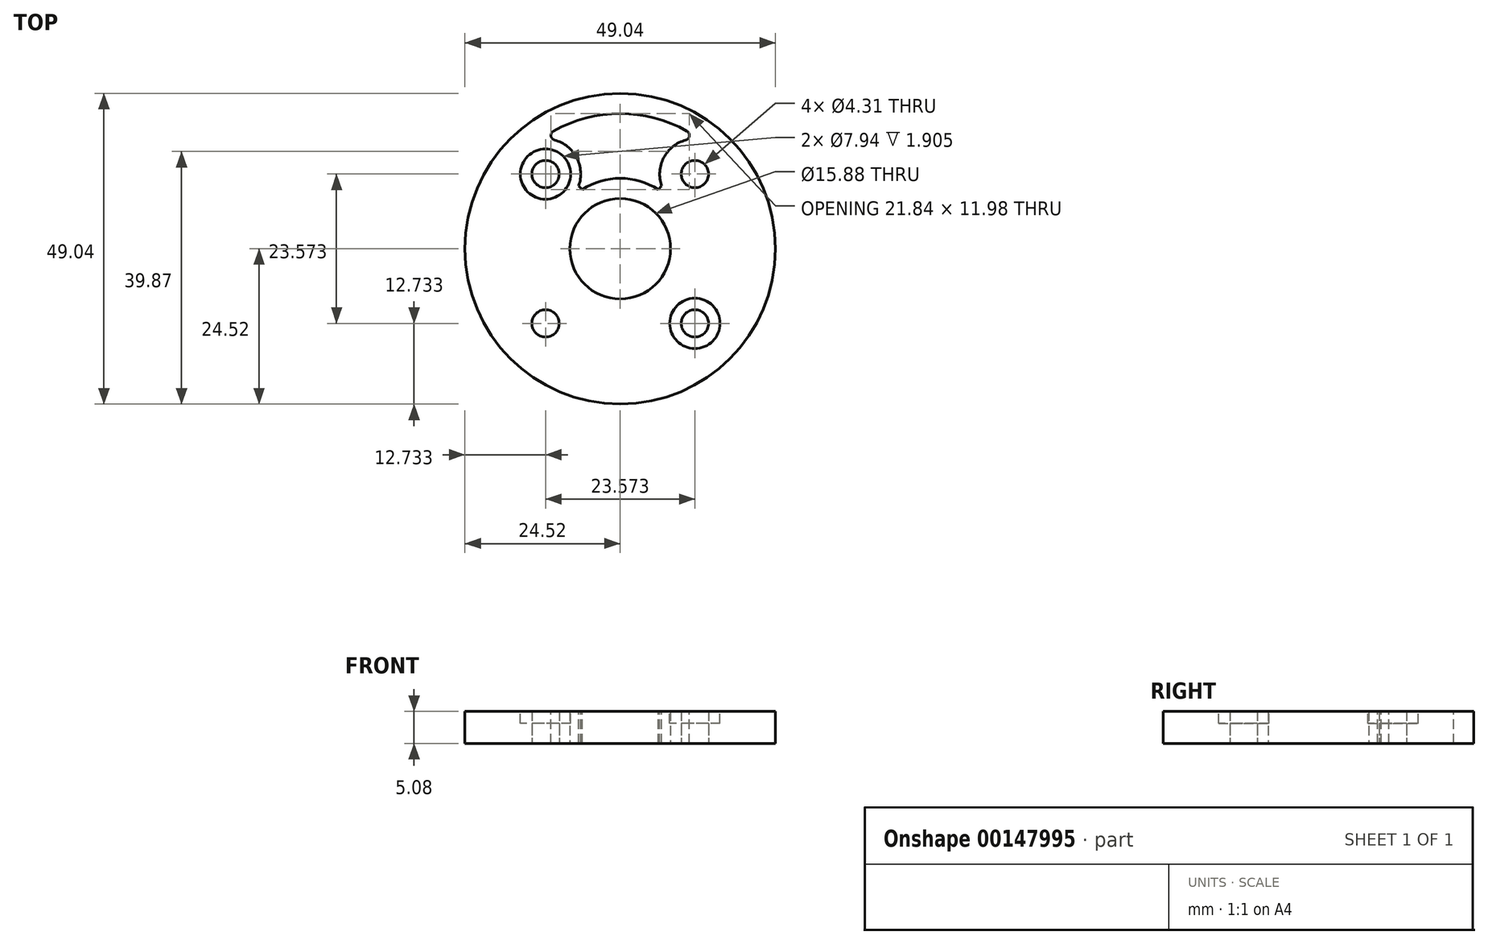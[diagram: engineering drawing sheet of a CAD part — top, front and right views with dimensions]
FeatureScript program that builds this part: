
annotation { "Feature Type Name" : "Feature", "Feature Type Description" : "" }
export const myFeature = defineFeature(function(context is Context, id is Id, definition is map)
    precondition{}
    {
        {
            var Q0;
            Q0=qCreatedBy(makeId("Top.planeOp"),FACE);
            var sketch = newSketch(context, id + "F0", { "sketchPlane" : qUnion([Q0])});
            skCircle(sketch, "E0", {"center": v(0, 0) * mm, "radius": 24.52 * mm});
            skCircle(sketch, "E1", {"center": v(0, 0) * mm, "radius": 7.94 * mm});
            skLineSegment(sketch, "E2.bottom", {"start": v(-11.79, 11.79) * mm, "end": v(11.79, 11.79) * mm, "construction": true});
            skLineSegment(sketch, "E2.top", {"start": v(-11.79, -11.79) * mm, "end": v(11.79, -11.79) * mm, "construction": true});
            skLineSegment(sketch, "E2.left", {"start": v(-11.79, 11.79) * mm, "end": v(-11.79, -11.79) * mm, "construction": true});
            skLineSegment(sketch, "E2.right", {"start": v(11.79, 11.79) * mm, "end": v(11.79, -11.79) * mm, "construction": true});
            skCircle(sketch, "E3", {"center": v(-11.79, 11.79) * mm, "radius": 7.85 * mm, "construction": true});
            skCircle(sketch, "E4", {"center": v(11.79, 11.79) * mm, "radius": 2.15 * mm});
            skCircle(sketch, "E5", {"center": v(-11.79, 11.79) * mm, "radius": 2.15 * mm});
            skCircle(sketch, "E6", {"center": v(-11.79, -11.79) * mm, "radius": 2.15 * mm});
            skCircle(sketch, "E7", {"center": v(11.79, -11.79) * mm, "radius": 2.15 * mm});
            skCircle(sketch, "E8", {"center": v(-11.79, -11.79) * mm, "radius": 3.97 * mm, "construction": true});
            skCircle(sketch, "E9", {"center": v(11.79, 11.79) * mm, "radius": 3.97 * mm, "construction": true});
            skSolve(sketch);
        }
        {
            var Q0;
            Q0=qSketchRegion(id+"F0",true);
            extrude(context, id + "F1", {"entities" : qUnion([Q0]), "depth" : 5.08 * mm});
        }
        {
            var Q0;
            Q0=makeQuery(id+"F1.opExtrude","CAP_FACE",FACE,{"disambiguationData":[OSD([sQuery(id+"F0.wireOp",EDGE,"E0"),sQuery(id+"F0.wireOp",EDGE,"E1"),sQuery(id+"F0.wireOp",EDGE,"E4"),sQuery(id+"F0.wireOp",EDGE,"E5"),sQuery(id+"F0.wireOp",EDGE,"E6"),sQuery(id+"F0.wireOp",EDGE,"E7")])],"isStart":false});
            var sketch = newSketch(context, id + "F2", { "sketchPlane" : qUnion([Q0])});
            skArc(sketch, "E10", {"start": v(-6.55, 9.92) * mm, "mid": v(-7.46, 15.27) * mm, "end": v(-12.5, 17.3) * mm});
            skArc(sketch, "E11", {"start": v(12.5, 17.3) * mm, "mid": v(7.46, 15.27) * mm, "end": v(6.55, 9.92) * mm});
            skArc(sketch, "E12", {"start": v(12.5, 17.3) * mm, "mid": v(0, 21.34) * mm, "end": v(-12.5, 17.3) * mm});
            skArc(sketch, "E13", {"start": v(6, 9.36) * mm, "mid": v(0, 11.11) * mm, "end": v(-6, 9.36) * mm});
            skLineSegment(sketch, "E14.bottom", {"start": v(-9.92, 6.55) * mm, "end": v(-6.55, 9.92) * mm, "construction": true});
            skLineSegment(sketch, "E14.top", {"start": v(-9.36, 6) * mm, "end": v(-6, 9.36) * mm, "construction": true});
            skLineSegment(sketch, "E14.left", {"start": v(-9.92, 6.55) * mm, "end": v(-9.36, 6) * mm, "construction": true});
            skLineSegment(sketch, "E14.right", {"start": v(-6.55, 9.92) * mm, "end": v(-6, 9.36) * mm});
            skLineSegment(sketch, "E15.bottom", {"start": v(9.92, 6.55) * mm, "end": v(6.55, 9.92) * mm, "construction": true});
            skLineSegment(sketch, "E15.top", {"start": v(9.36, 6) * mm, "end": v(6, 9.36) * mm, "construction": true});
            skLineSegment(sketch, "E15.left", {"start": v(9.92, 6.55) * mm, "end": v(9.36, 6) * mm, "construction": true});
            skLineSegment(sketch, "E15.right", {"start": v(6.55, 9.92) * mm, "end": v(6, 9.36) * mm});
            skLineSegment(sketch, "E16", {"start": v(-8.24, 8.24) * mm, "end": v(-11.79, 11.79) * mm, "construction": true});
            skLineSegment(sketch, "E17", {"start": v(-7.68, 7.68) * mm, "end": v(0, 0) * mm, "construction": true});
            skLineSegment(sketch, "E18", {"start": v(0, 0) * mm, "end": v(7.68, 7.68) * mm, "construction": true});
            skLineSegment(sketch, "E19", {"start": v(8.24, 8.24) * mm, "end": v(11.79, 11.79) * mm, "construction": true});
            skSolve(sketch);
        }
        {
            var Q0;
            Q0=makeQuery(id+"F2.imprint","IMPRINT",FACE,{"disambiguationData":[TD([[makeQuery(id+"F2.imprint","IMPRINT",EDGE,{"derivedFrom":sQuery(id+"F2.wireOp",EDGE,"E10")}),-1.0]])]});
            var Q1;
            Q1=makeQuery(id+"F1.opExtrude","CAP_FACE",FACE,{"disambiguationData":[OSD([sQuery(id+"F0.wireOp",EDGE,"E0"),sQuery(id+"F0.wireOp",EDGE,"E1"),sQuery(id+"F0.wireOp",EDGE,"E4"),sQuery(id+"F0.wireOp",EDGE,"E5"),sQuery(id+"F0.wireOp",EDGE,"E6"),sQuery(id+"F0.wireOp",EDGE,"E7")])],"isStart":true});
            extrude(context, id + "F3", {"entities" : qUnion([Q0]), "operationType" : NewBodyOperationType.REMOVE, "endBound" : BoundingType.UP_TO_SURFACE, "oppositeDirection" : true, "endBoundEntityFace" : qUnion([Q1]), "depth" : 25.4 * mm});
        }
        {
            var Q0;
            Q0=makeQuery(id+"F6MqURjXbY15YYN_1.1.F3.boolean.opBoolean","COPY",EDGE,{"derivedFrom":makeQuery(id+"F6MqURjXbY15YYN_1.1.F3.opExtrude","SWEPT_EDGE",EDGE,{"disambiguationData":[OSD([sQuery(id+"F2.wireOp",EDGE,"E10"),sQuery(id+"F2.wireOp",EDGE,"E12")])]})});
            var Q1;
            Q1=makeQuery(id+"F6MqURjXbY15YYN_1.1.F3.boolean.opBoolean","COPY",EDGE,{"derivedFrom":makeQuery(id+"F6MqURjXbY15YYN_1.1.F3.opExtrude","SWEPT_EDGE",EDGE,{"disambiguationData":[OSD([sQuery(id+"F2.wireOp",EDGE,"E11"),sQuery(id+"F2.wireOp",EDGE,"E12")])]})});
            var Q2;
            Q2=makeQuery(id+"F6MqURjXbY15YYN_1.2.F3.boolean.opBoolean","COPY",EDGE,{"derivedFrom":makeQuery(id+"F6MqURjXbY15YYN_1.2.F3.opExtrude","SWEPT_EDGE",EDGE,{"disambiguationData":[OSD([sQuery(id+"F2.wireOp",EDGE,"E10"),sQuery(id+"F2.wireOp",EDGE,"E12")])]})});
            var Q3;
            Q3=makeQuery(id+"F6MqURjXbY15YYN_1.2.F3.boolean.opBoolean","COPY",EDGE,{"derivedFrom":makeQuery(id+"F6MqURjXbY15YYN_1.2.F3.opExtrude","SWEPT_EDGE",EDGE,{"disambiguationData":[OSD([sQuery(id+"F2.wireOp",EDGE,"E11"),sQuery(id+"F2.wireOp",EDGE,"E12")])]})});
            var Q4;
            Q4=makeQuery(id+"F6MqURjXbY15YYN_1.3.F3.boolean.opBoolean","COPY",EDGE,{"derivedFrom":makeQuery(id+"F6MqURjXbY15YYN_1.3.F3.opExtrude","SWEPT_EDGE",EDGE,{"disambiguationData":[OSD([sQuery(id+"F2.wireOp",EDGE,"E10"),sQuery(id+"F2.wireOp",EDGE,"E12")])]})});
            var Q5;
            Q5=makeQuery(id+"F6MqURjXbY15YYN_1.3.F3.boolean.opBoolean","COPY",EDGE,{"derivedFrom":makeQuery(id+"F6MqURjXbY15YYN_1.3.F3.opExtrude","SWEPT_EDGE",EDGE,{"disambiguationData":[OSD([sQuery(id+"F2.wireOp",EDGE,"E11"),sQuery(id+"F2.wireOp",EDGE,"E12")])]})});
            var Q6;
            Q6=makeQuery(id+"F3.boolean.opBoolean","COPY",EDGE,{"derivedFrom":makeQuery(id+"F3.opExtrude","SWEPT_EDGE",EDGE,{"disambiguationData":[OSD([sQuery(id+"F2.wireOp",EDGE,"E10"),sQuery(id+"F2.wireOp",EDGE,"E12")])]})});
            var Q7;
            Q7=makeQuery(id+"F3.boolean.opBoolean","COPY",EDGE,{"derivedFrom":makeQuery(id+"F3.opExtrude","SWEPT_EDGE",EDGE,{"disambiguationData":[OSD([sQuery(id+"F2.wireOp",EDGE,"E11"),sQuery(id+"F2.wireOp",EDGE,"E12")])]})});
            fillet(context, id + "F4", {"entities" : qUnion([Q0, Q1, Q2, Q3, Q4, Q5, Q6, Q7]), "radius" : 0.76 * mm, "tangentPropagation" : true, "allowEdgeOverflow" : false});
        }
        {
            var Q0;
            Q0=makeQuery(id+"F1.opExtrude","CAP_FACE",FACE,{"disambiguationData":[OSD([sQuery(id+"F0.wireOp",EDGE,"E0"),sQuery(id+"F0.wireOp",EDGE,"E1"),sQuery(id+"F0.wireOp",EDGE,"E4"),sQuery(id+"F0.wireOp",EDGE,"E5"),sQuery(id+"F0.wireOp",EDGE,"E6"),sQuery(id+"F0.wireOp",EDGE,"E7")])],"isStart":false});
            var sketch = newSketch(context, id + "F5", { "sketchPlane" : qUnion([Q0])});
            skCircle(sketch, "E20", {"center": v(-11.79, 11.79) * mm, "radius": 3.97 * mm});
            skCircle(sketch, "E21", {"center": v(11.79, -11.79) * mm, "radius": 3.97 * mm});
            skSolve(sketch);
        }
        {
            var Q0;
            Q0=qSketchRegion(id+"F5",true);
            extrude(context, id + "F6", {"entities" : qUnion([Q0]), "operationType" : NewBodyOperationType.REMOVE, "oppositeDirection" : true, "depth" : 1.9 * mm});
        }
    });
